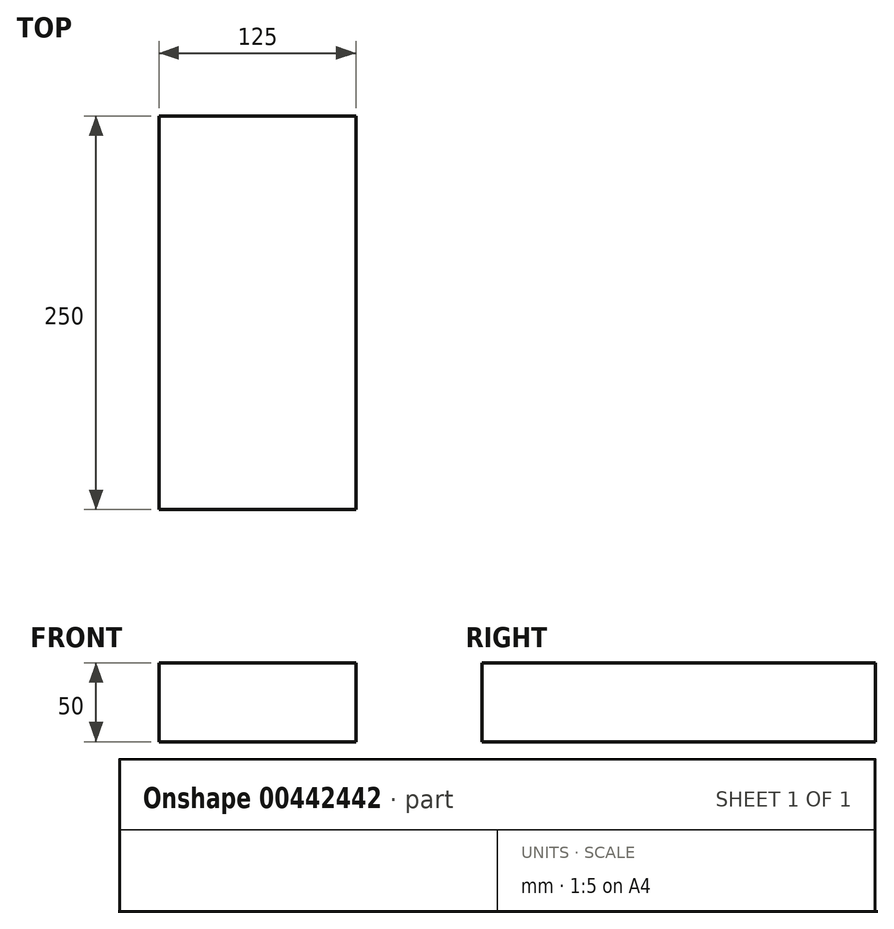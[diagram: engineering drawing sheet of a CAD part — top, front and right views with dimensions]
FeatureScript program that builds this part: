
annotation { "Feature Type Name" : "Feature", "Feature Type Description" : "" }
export const myFeature = defineFeature(function(context is Context, id is Id, definition is map)
    precondition{}
    {
        {
            var Q0;
            Q0=qCreatedBy(makeId("Front.planeOp"),FACE);
            var sketch = newSketch(context, id + "F0", { "sketchPlane" : qUnion([Q0])});
            skLineSegment(sketch, "E0.bottom", {"start": v(62.5, 25) * mm, "end": v(-62.5, 25) * mm});
            skLineSegment(sketch, "E0.top", {"start": v(62.5, -25) * mm, "end": v(-62.5, -25) * mm});
            skLineSegment(sketch, "E0.left", {"start": v(62.5, 25) * mm, "end": v(62.5, -25) * mm});
            skLineSegment(sketch, "E0.right", {"start": v(-62.5, 25) * mm, "end": v(-62.5, -25) * mm});
            skPoint(sketch, "E0.middle", {"position": v(0, 0) * mm});
            skSolve(sketch);
        }
        {
            var Q0;
            Q0=makeQuery(id+"F0.imprint","IMPRINT",FACE,{"disambiguationData":[TD([[makeQuery(id+"F0.imprint","IMPRINT",EDGE,{"derivedFrom":sQuery(id+"F0.wireOp",EDGE,"E0.bottom")}),1.0]])]});
            extrude(context, id + "F1", {"entities" : qUnion([Q0]), "endBound" : BoundingType.SYMMETRIC, "depth" : 250 * mm});
        }
    });
